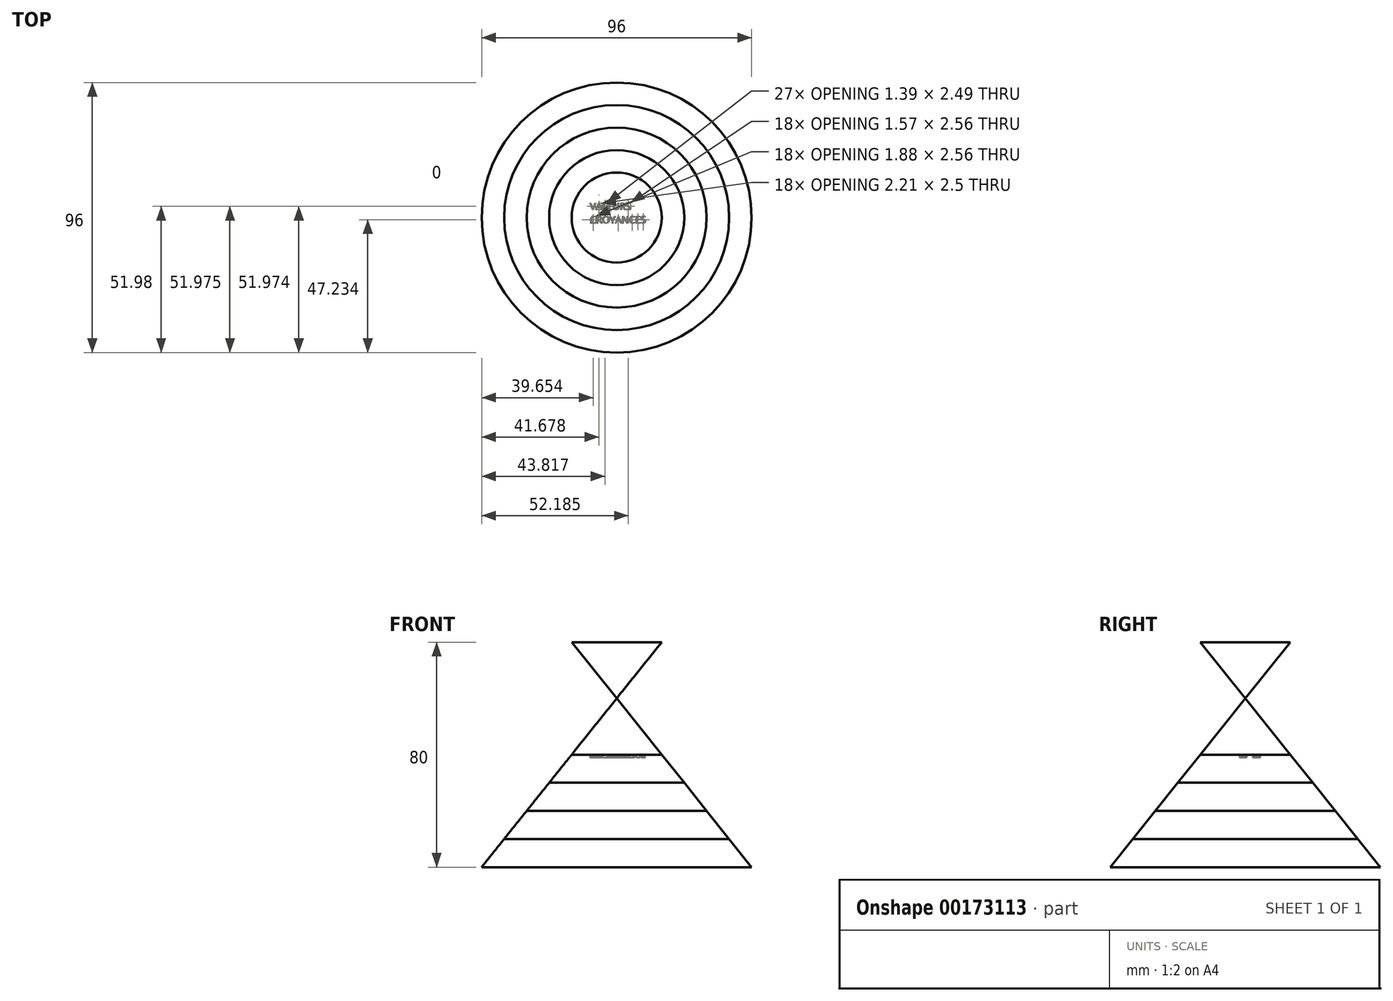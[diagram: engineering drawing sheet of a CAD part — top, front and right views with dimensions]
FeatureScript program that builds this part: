
annotation { "Feature Type Name" : "Feature", "Feature Type Description" : "" }
export const myFeature = defineFeature(function(context is Context, id is Id, definition is map)
    precondition{}
    {
        {
            var Q0;
            Q0=qCreatedBy(makeId("Front.planeOp"),FACE);
            var sketch = newSketch(context, id + "F0", { "sketchPlane" : qUnion([Q0])});
            skLineSegment(sketch, "E0", {"start": v(0, 0) * mm, "end": v(48, 0) * mm});
            skLineSegment(sketch, "E1", {"start": v(48, 0) * mm, "end": v(-16, 80) * mm});
            skLineSegment(sketch, "E2", {"start": v(-16, 80) * mm, "end": v(0, 80) * mm});
            skLineSegment(sketch, "E3", {"start": v(0, 60) * mm, "end": v(0, 80) * mm});
            skLineSegment(sketch, "E4", {"start": v(0, 0) * mm, "end": v(0, 10) * mm});
            skLineSegment(sketch, "E5", {"start": v(0, 10) * mm, "end": v(40, 10) * mm});
            skLineSegment(sketch, "E6", {"start": v(0, 10) * mm, "end": v(0, 20) * mm});
            skLineSegment(sketch, "E7", {"start": v(0, 20) * mm, "end": v(32, 20) * mm});
            skLineSegment(sketch, "E8", {"start": v(0, 20) * mm, "end": v(0, 30) * mm});
            skLineSegment(sketch, "E9", {"start": v(0, 30) * mm, "end": v(24, 30) * mm});
            skLineSegment(sketch, "E10", {"start": v(0, 30) * mm, "end": v(0, 40) * mm});
            skLineSegment(sketch, "E11", {"start": v(0, 40) * mm, "end": v(16, 40) * mm});
            skLineSegment(sketch, "E12", {"start": v(0, 40) * mm, "end": v(0, 60) * mm});
            skSolve(sketch);
        }
        {
            var Q0;
            {var subQ0=sQuery(id+"F0.wireOp",EDGE,"E0");Q0=makeQuery(id+"F0.imprint","IMPRINT",FACE,{"disambiguationData":[TD([[makeQuery(id+"F0.imprint","IMPRINT",EDGE,{"derivedFrom":subQ0}),1.0]])]});}
            var Q1;
            Q1=sQuery(id+"F0.wireOp",EDGE,"E4");
            revolve(context, id + "F1", {"entities" : qUnion([Q0]), "axis" : qUnion([Q1]), "revolveType" : RevolveType.FULL});
        }
        {
            var Q0;
            {var subQ0=sQuery(id+"F0.wireOp",EDGE,"E5");Q0=makeQuery(id+"F0.imprint","IMPRINT",FACE,{"disambiguationData":[TD([[makeQuery(id+"F0.imprint","IMPRINT",EDGE,{"derivedFrom":subQ0}),1.0]])]});}
            var Q1;
            Q1=sQuery(id+"F0.wireOp",EDGE,"E6");
            revolve(context, id + "F2", {"entities" : qUnion([Q0]), "axis" : qUnion([Q1]), "revolveType" : RevolveType.FULL});
        }
        {
            var Q0;
            {var subQ0=sQuery(id+"F0.wireOp",EDGE,"E7");Q0=makeQuery(id+"F0.imprint","IMPRINT",FACE,{"disambiguationData":[TD([[makeQuery(id+"F0.imprint","IMPRINT",EDGE,{"derivedFrom":subQ0}),1.0]])]});}
            var Q1;
            Q1=sQuery(id+"F0.wireOp",EDGE,"E8");
            revolve(context, id + "F3", {"entities" : qUnion([Q0]), "axis" : qUnion([Q1]), "revolveType" : RevolveType.FULL});
        }
        {
            var Q0;
            {var subQ0=sQuery(id+"F0.wireOp",EDGE,"E9");Q0=makeQuery(id+"F0.imprint","IMPRINT",FACE,{"disambiguationData":[TD([[makeQuery(id+"F0.imprint","IMPRINT",EDGE,{"derivedFrom":subQ0}),1.0]])]});}
            var Q1;
            Q1=sQuery(id+"F0.wireOp",EDGE,"E10");
            revolve(context, id + "F4", {"entities" : qUnion([Q0]), "axis" : qUnion([Q1]), "revolveType" : RevolveType.FULL});
        }
        {
            var Q0;
            {var subQ2=sQuery(id+"F0.wireOp",EDGE,"E11");Q0=makeQuery(id+"F0.imprint","IMPRINT",FACE,{"disambiguationData":[TD([[makeQuery(id+"F0.imprint","IMPRINT",EDGE,{"derivedFrom":subQ2}),1.0]])]});}
            var Q1;
            Q1=sQuery(id+"F0.wireOp",EDGE,"E12");
            revolve(context, id + "F5", {"entities" : qUnion([Q0]), "axis" : qUnion([Q1]), "revolveType" : RevolveType.FULL});
        }
        {
            var Q0;
            {var subQ0=sQuery(id+"F0.wireOp",EDGE,"E2");Q0=makeQuery(id+"F0.imprint","IMPRINT",FACE,{"disambiguationData":[TD([[makeQuery(id+"F0.imprint","IMPRINT",EDGE,{"derivedFrom":subQ0}),-1.0]])]});}
            var Q1;
            Q1=sQuery(id+"F0.wireOp",EDGE,"E3");
            revolve(context, id + "F6", {"entities" : qUnion([Q0]), "axis" : qUnion([Q1]), "revolveType" : RevolveType.FULL});
        }
        {
            var Q0;
            Q0=makeQuery(id+"F4.opRevolve","SWEPT_FACE",FACE,{"disambiguationData":[OSD([sQuery(id+"F0.wireOp",EDGE,"E11")])]});
            var sketch = newSketch(context, id + "F7", { "sketchPlane" : qUnion([Q0])});
            skText(sketch, "E13", { "text": "VALEURS\nCROYANCES", "fontName": "OpenSans-Regular.ttf"});
            const initialGuessF7  = {"E13": [-0.0095, 0.00273, 1, 0, 0.00251]};
            skSetInitialGuess(sketch, initialGuessF7);
            skSolve(sketch);
        }
        {
            var Q0;
            Q0 = qSketchRegion(id + "F7", true);
            extrude(context, id + "F8", {"entities" : qUnion([Q0]), "operationType" : NewBodyOperationType.REMOVE, "oppositeDirection" : true, "depth" : 1 * mm});
        }
    });
